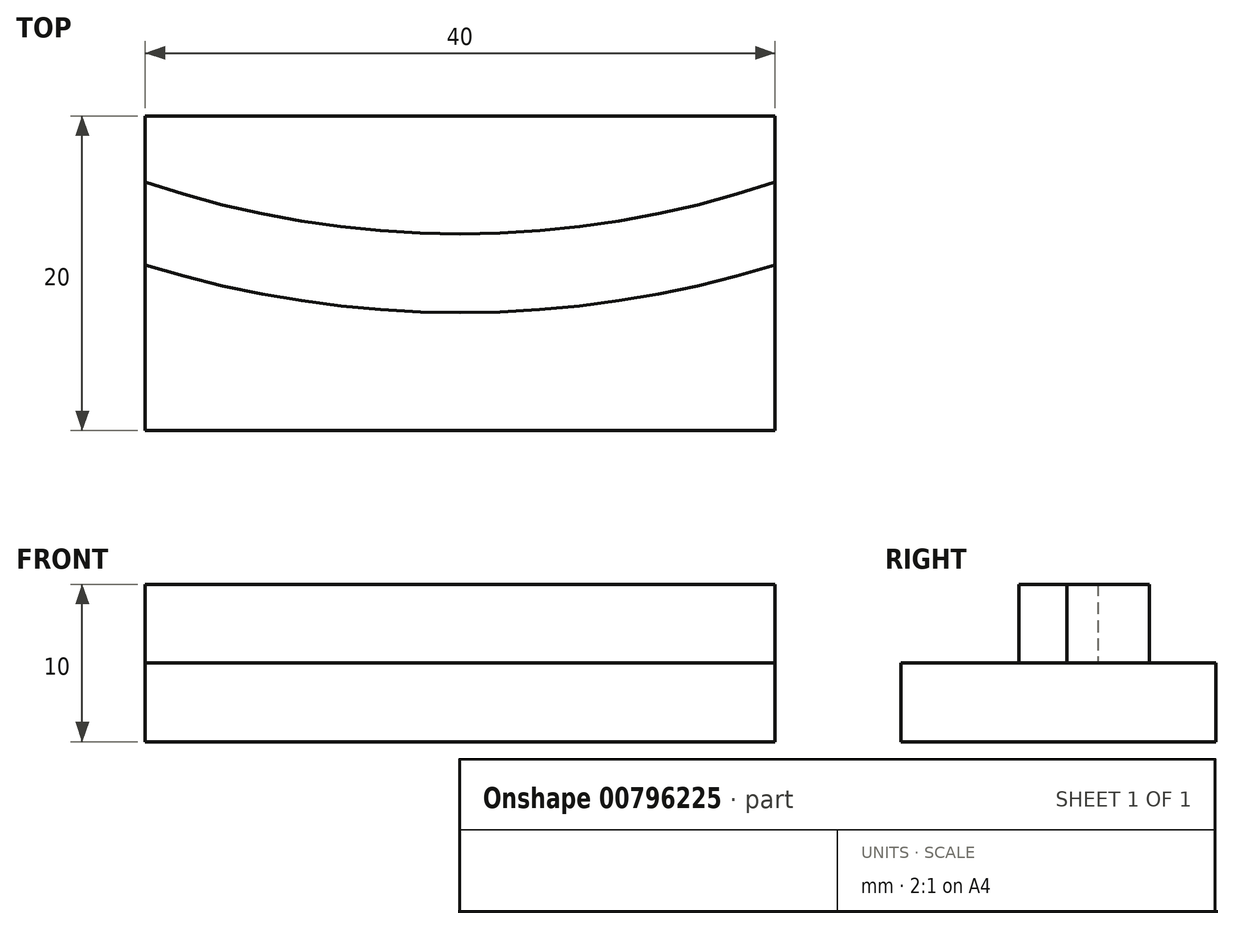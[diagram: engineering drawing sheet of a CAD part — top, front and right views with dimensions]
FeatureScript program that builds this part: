
annotation { "Feature Type Name" : "Feature", "Feature Type Description" : "" }
export const myFeature = defineFeature(function(context is Context, id is Id, definition is map)
    precondition{}
    {
        {
            var Q0;
            Q0=qCreatedBy(makeId("Top.planeOp"),FACE);
            var sketch = newSketch(context, id + "F0", { "sketchPlane" : qUnion([Q0])});
            skLineSegment(sketch, "E0", {"start": v(0, 0) * mm, "end": v(40, 0) * mm});
            skLineSegment(sketch, "E1", {"start": v(40, 0) * mm, "end": v(40, 20) * mm});
            skLineSegment(sketch, "E2", {"start": v(40, 20) * mm, "end": v(0, 20) * mm});
            skLineSegment(sketch, "E3", {"start": v(0, 20) * mm, "end": v(0, 0) * mm});
            skSolve(sketch);
        }
        {
            var Q0;
            Q0 = qSketchRegion(id + "F0", true);
            extrude(context, id + "F1", {"entities" : qUnion([Q0]), "depth" : 5 * mm, "offsetDistance" : 25 * mm});
        }
        {
            var Q0;
            Q0=makeQuery(id+"F1.opExtrude","CAP_FACE",FACE,{"disambiguationData":[OSD([sQuery(id+"F0.wireOp",EDGE,"E0"),sQuery(id+"F0.wireOp",EDGE,"E1"),sQuery(id+"F0.wireOp",EDGE,"E2"),sQuery(id+"F0.wireOp",EDGE,"E3")])],"isStart":false});
            var sketch = newSketch(context, id + "F2", { "sketchPlane" : qUnion([Q0])});
            skCircle(sketch, "E4", {"center": v(20, 75) * mm, "radius": 65 * mm, "construction": true});
            skPoint(sketch, "E4.centerSnap0", {"position": v(20, 20) * mm});
            skCircle(sketch, "E5", {"center": v(20, 75) * mm, "radius": 67.5 * mm, "construction": true});
            skCircle(sketch, "E6", {"center": v(20, 75) * mm, "radius": 62.5 * mm, "construction": true});
            skLineSegment(sketch, "E7", {"start": v(0, 10.53) * mm, "end": v(0, 15.79) * mm});
            skLineSegment(sketch, "E8", {"start": v(40, 15.79) * mm, "end": v(40, 10.53) * mm});
            skArc(sketch, "E9", {"start": v(40, 15.79) * mm, "mid": v(20, 12.5) * mm, "end": v(0, 15.79) * mm});
            skArc(sketch, "E10", {"start": v(40, 10.53) * mm, "mid": v(20, 7.5) * mm, "end": v(0, 10.53) * mm});
            skSolve(sketch);
        }
        {
            var Q0;
            Q0 = qSketchRegion(id + "F2", true);
            extrude(context, id + "F3", {"entities" : qUnion([Q0]), "depth" : 5 * mm, "offsetDistance" : 25 * mm});
        }
    });
